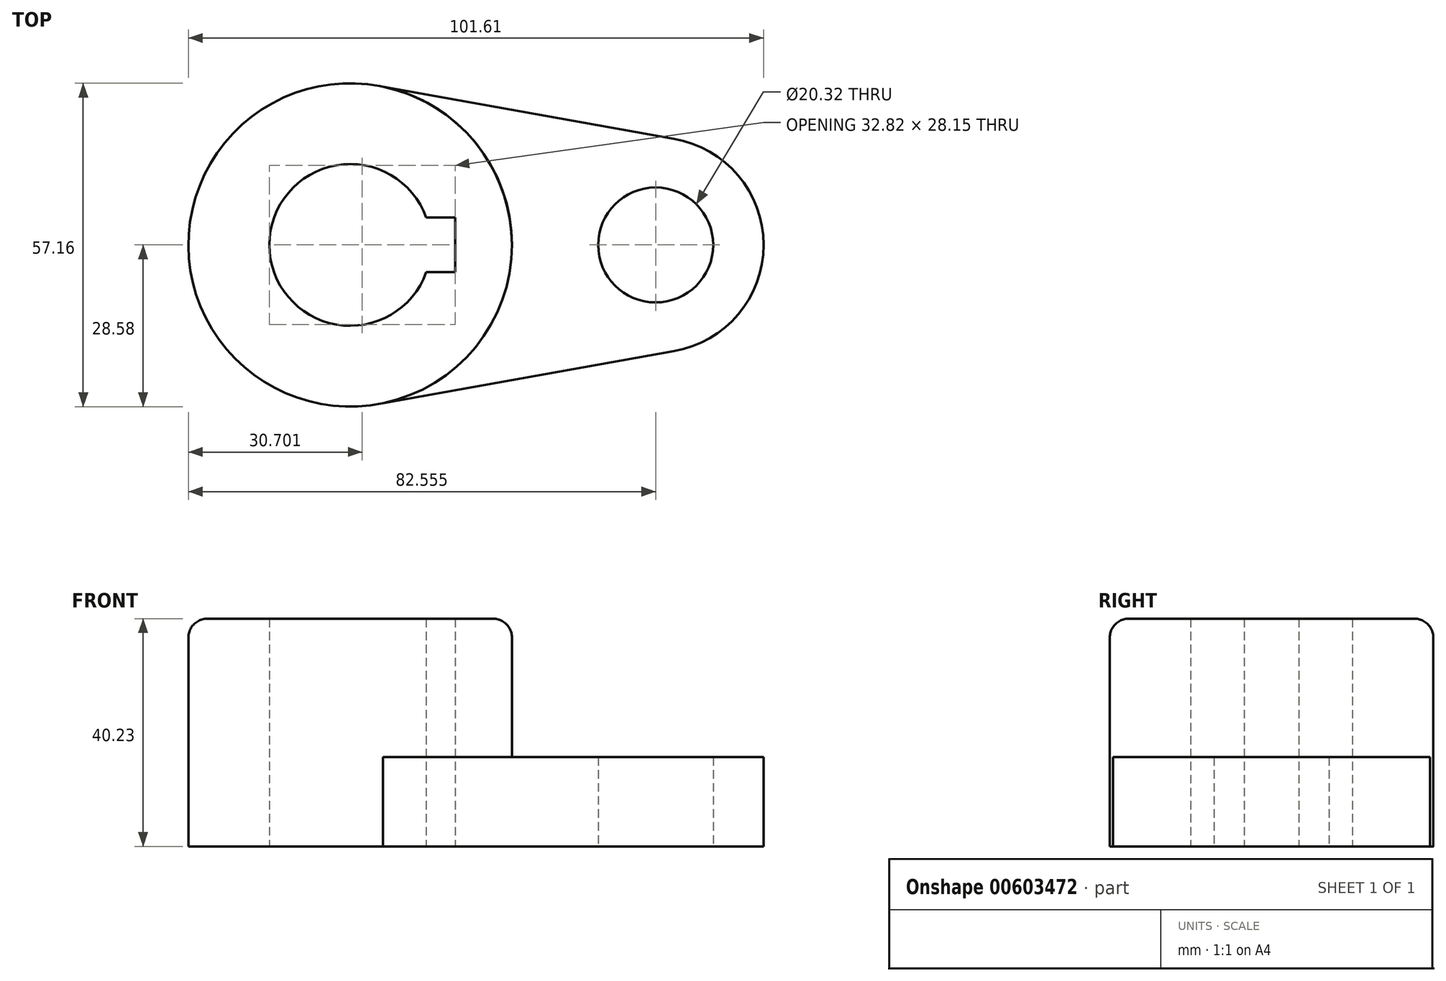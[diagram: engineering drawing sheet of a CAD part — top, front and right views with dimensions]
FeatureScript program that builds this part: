
annotation { "Feature Type Name" : "Feature", "Feature Type Description" : "" }
export const myFeature = defineFeature(function(context is Context, id is Id, definition is map)
    precondition{}
    {
        {
            var Q0;
            Q0=qCreatedBy(makeId("Top.planeOp"),FACE);
            var sketch = newSketch(context, id + "F0", { "sketchPlane" : qUnion([Q0])});
            skArc(sketch, "E0", {"start": v(13.45, 4.83) * mm, "mid": v(-14.29, 0) * mm, "end": v(13.45, -4.83) * mm});
            skPoint(sketch, "E1.start.orphan", {"position": v(14.29, 0) * mm});
            skLineSegment(sketch, "E2", {"start": v(18.53, 4.83) * mm, "end": v(18.53, -4.83) * mm});
            skCircle(sketch, "E3", {"center": v(0, 0) * mm, "radius": 28.58 * mm});
            skLineSegment(sketch, "E4", {"start": v(13.45, 4.83) * mm, "end": v(18.53, 4.83) * mm});
            skLineSegment(sketch, "E5", {"start": v(18.53, -4.83) * mm, "end": v(13.45, -4.83) * mm});
            skSolve(sketch);
        }
        {
            var Q0;
            Q0=makeQuery(id+"F0.imprint","IMPRINT",FACE,{"disambiguationData":[TD([[makeQuery(id+"F0.imprint","IMPRINT",EDGE,{"derivedFrom":sQuery(id+"F0.wireOp",EDGE,"E0")}),-1.0]])]});
            extrude(context, id + "F1", {"entities" : qUnion([Q0]), "depth" : 40.23 * mm, "offsetDistance" : 25.4 * mm});
        }
        {
            var Q0;
            Q0=makeQuery(id+"F1.opExtrude","CAP_EDGE",EDGE,{"disambiguationData":[OSD([sQuery(id+"F0.wireOp",EDGE,"E3")])],"isStart":false});
            fillet(context, id + "F2", {"entities" : qUnion([Q0]), "radius" : 3.3 * mm, "tangentPropagation" : true, "allowEdgeOverflow" : false});
        }
        {
            var Q0;
            Q0=makeQuery(id+"F1.opExtrude","CAP_FACE",FACE,{"disambiguationData":[OSD([sQuery(id+"F0.wireOp",EDGE,"E0"),sQuery(id+"F0.wireOp",EDGE,"E2"),sQuery(id+"F0.wireOp",EDGE,"E3"),sQuery(id+"F0.wireOp",EDGE,"E4"),sQuery(id+"F0.wireOp",EDGE,"E5")])],"isStart":true});
            var sketch = newSketch(context, id + "F3", { "sketchPlane" : qUnion([Q0])});
            skCircle(sketch, "E6", {"center": v(53.98, 0) * mm, "radius": 10.16 * mm});
            skArc(sketch, "E7", {"start": v(57.2, -18.78) * mm, "mid": v(73.03, 0) * mm, "end": v(57.2, 18.78) * mm});
            skLineSegment(sketch, "E8", {"start": v(57.2, 18.78) * mm, "end": v(4.27, 28.25) * mm});
            skPoint(sketch, "E9.start.orphan", {"position": v(0, 28.58) * mm});
            skLineSegment(sketch, "E10.MirrorCS", {"start": v(57.2, -18.78) * mm, "end": v(4.27, -28.25) * mm});
            skSolve(sketch);
        }
        {
            var Q0;
            Q0=makeQuery(id+"F3.imprint","IMPRINT",FACE,{"disambiguationData":[TD([[makeQuery(id+"F3.imprint","IMPRINT",EDGE,{"derivedFrom":sQuery(id+"F3.wireOp",EDGE,"E6")}),-1.0]])]});
            extrude(context, id + "F4", {"entities" : qUnion([Q0]), "operationType" : NewBodyOperationType.ADD, "oppositeDirection" : true, "depth" : 15.77 * mm, "offsetDistance" : 25.4 * mm});
        }
    });
